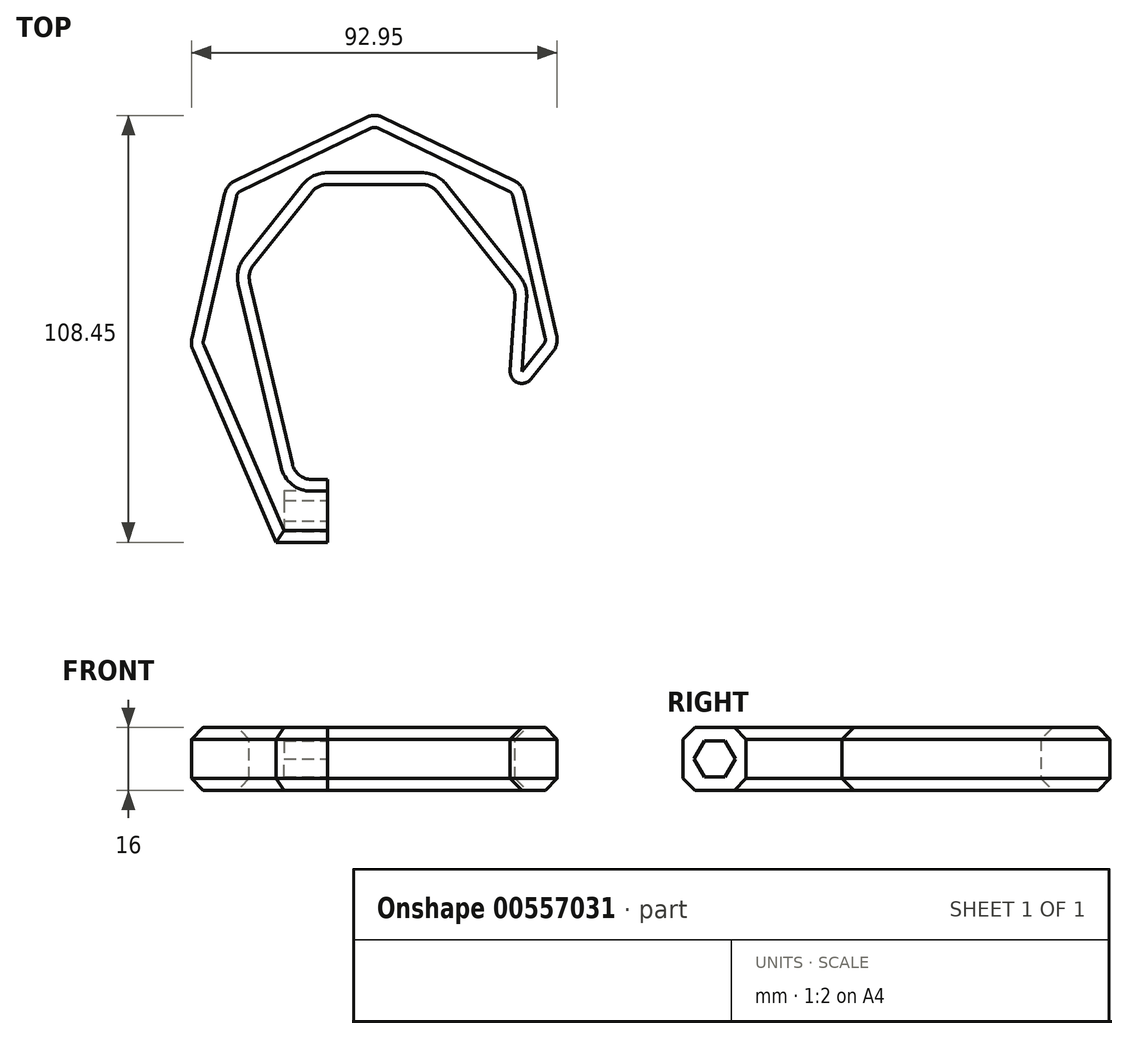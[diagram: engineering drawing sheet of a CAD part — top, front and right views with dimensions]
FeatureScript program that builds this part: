
annotation { "Feature Type Name" : "Feature", "Feature Type Description" : "" }
export const myFeature = defineFeature(function(context is Context, id is Id, definition is map)
    precondition{}
    {
        {
            var Q0;
            Q0=qCreatedBy(makeId("Top.planeOp"),FACE);
            var sketch = newSketch(context, id + "F0", { "sketchPlane" : qUnion([Q0])});
            skLineSegment(sketch, "E0", {"start": v(0, -45) * mm, "end": v(-20, -45) * mm});
            skLineSegment(sketch, "E1", {"start": v(0, -45) * mm, "end": v(0, -61) * mm});
            skLineSegment(sketch, "E2", {"start": v(0, -61) * mm, "end": v(-25, -61) * mm});
            skCircle(sketch, "E3.cCircle", {"center": v(0, 0) * mm, "radius": 43.25 * mm, "construction": true});
            skLineSegment(sketch, "E3.0", {"start": v(46.8, -10.68) * mm, "end": v(20.83, -43.25) * mm});
            skLineSegment(sketch, "E3.1", {"start": v(20.83, -43.25) * mm, "end": v(-20.83, -43.25) * mm});
            skLineSegment(sketch, "E3.2", {"start": v(-20.83, -43.25) * mm, "end": v(-46.8, -10.68) * mm});
            skLineSegment(sketch, "E3.3", {"start": v(-46.8, -10.68) * mm, "end": v(-37.53, 29.93) * mm});
            skLineSegment(sketch, "E3.4", {"start": v(-37.53, 29.93) * mm, "end": v(0, 48) * mm});
            skLineSegment(sketch, "E3.5", {"start": v(0, 48) * mm, "end": v(37.53, 29.93) * mm});
            skLineSegment(sketch, "E3.6", {"start": v(37.53, 29.93) * mm, "end": v(46.8, -10.68) * mm});
            skPoint(sketch, "E3.0.midPoint", {"position": v(33.81, -26.96) * mm});
            skLineSegment(sketch, "E4", {"start": v(-20, -45) * mm, "end": v(-37.53, 29.93) * mm});
            skLineSegment(sketch, "E5", {"start": v(-25, -61) * mm, "end": v(-46.8, -10.68) * mm});
            skLineSegment(sketch, "E6", {"start": v(-46.8, -10.68) * mm, "end": v(0, 48) * mm});
            skLineSegment(sketch, "E7", {"start": v(-37.53, 29.93) * mm, "end": v(37.53, 29.93) * mm});
            skLineSegment(sketch, "E8", {"start": v(0, 48) * mm, "end": v(46.8, -10.68) * mm});
            skLineSegment(sketch, "E9", {"start": v(37.53, 29.93) * mm, "end": v(33.81, -26.96) * mm});
            skSolve(sketch);
        }
        {
            var Q0;
            {var subQ4=sQuery(id+"F0.wireOp",EDGE,"E0");Q0=makeQuery(id+"F0.imprint","IMPRINT",FACE,{"disambiguationData":[TD([[makeQuery(id+"F0.imprint","IMPRINT",EDGE,{"derivedFrom":subQ4}),1.0]])]});}
            var Q1;
            {var subQ0=sQuery(id+"F0.wireOp",EDGE,"E3.2");Q1=makeQuery(id+"F0.imprint","IMPRINT",FACE,{"disambiguationData":[TD([[makeQuery(id+"F0.imprint","IMPRINT",EDGE,{"derivedFrom":subQ0}),-1.0]])]});}
            var Q2;
            {var subQ0=sQuery(id+"F0.wireOp",EDGE,"E3.3");Q2=makeQuery(id+"F0.imprint","IMPRINT",FACE,{"disambiguationData":[TD([[makeQuery(id+"F0.imprint","IMPRINT",EDGE,{"derivedFrom":subQ0}),-1.0]])]});}
            var Q3;
            {var subQ1=sQuery(id+"F0.wireOp",EDGE,"E4");var subQ3=sQuery(id+"F0.wireOp",EDGE,"E6");var subQ4=makeQuery(id+"F0.imprint","INTERSECT",VERTEX,{"derivedFrom":[subQ1,subQ3]});Q3=makeQuery(id+"F0.imprint","IMPRINT",FACE,{"disambiguationData":[TD([[makeQuery(id+"F0.imprint","IMPRINT",EDGE,{"disambiguationData":[TD([[subQ4,-1.0]])],"derivedFrom":subQ3}),1.0]])]});}
            var Q4;
            {var subQ0=sQuery(id+"F0.wireOp",EDGE,"E3.4");Q4=makeQuery(id+"F0.imprint","IMPRINT",FACE,{"disambiguationData":[TD([[makeQuery(id+"F0.imprint","IMPRINT",EDGE,{"derivedFrom":subQ0}),-1.0]])]});}
            var Q5;
            {var subQ1=sQuery(id+"F0.wireOp",EDGE,"E6");var subQ3=sQuery(id+"F0.wireOp",EDGE,"E7");var subQ4=makeQuery(id+"F0.imprint","INTERSECT",VERTEX,{"derivedFrom":[subQ1,subQ3]});Q5=makeQuery(id+"F0.imprint","IMPRINT",FACE,{"disambiguationData":[TD([[makeQuery(id+"F0.imprint","IMPRINT",EDGE,{"disambiguationData":[TD([[subQ4,-1.0]])],"derivedFrom":subQ3}),1.0]])]});}
            var Q6;
            {var subQ0=sQuery(id+"F0.wireOp",EDGE,"E3.5");Q6=makeQuery(id+"F0.imprint","IMPRINT",FACE,{"disambiguationData":[TD([[makeQuery(id+"F0.imprint","IMPRINT",EDGE,{"derivedFrom":subQ0}),-1.0]])]});}
            var Q7;
            {var subQ1=sQuery(id+"F0.wireOp",EDGE,"E7");var subQ3=sQuery(id+"F0.wireOp",EDGE,"E8");var subQ4=makeQuery(id+"F0.imprint","INTERSECT",VERTEX,{"derivedFrom":[subQ1,subQ3]});Q7=makeQuery(id+"F0.imprint","IMPRINT",FACE,{"disambiguationData":[TD([[makeQuery(id+"F0.imprint","IMPRINT",EDGE,{"disambiguationData":[TD([[subQ4,-1.0]])],"derivedFrom":subQ3}),1.0]])]});}
            var Q8;
            {var subQ0=sQuery(id+"F0.wireOp",EDGE,"E3.6");Q8=makeQuery(id+"F0.imprint","IMPRINT",FACE,{"disambiguationData":[TD([[makeQuery(id+"F0.imprint","IMPRINT",EDGE,{"derivedFrom":subQ0}),-1.0]])]});}
            var Q9;
            {var subQ1=sQuery(id+"F0.wireOp",EDGE,"E3.0");var subQ3=sQuery(id+"F0.wireOp",EDGE,"E9");var subQ4=makeQuery(id+"F0.imprint","INTERSECT",VERTEX,{"derivedFrom":[subQ1,subQ3]});Q9=makeQuery(id+"F0.imprint","IMPRINT",FACE,{"disambiguationData":[TD([[makeQuery(id+"F0.imprint","IMPRINT",EDGE,{"disambiguationData":[TD([[subQ4,1.0]])],"derivedFrom":subQ3}),1.0]])]});}
            extrude(context, id + "F1", {"entities" : qUnion([Q0, Q1, Q2, Q3, Q4, Q5, Q6, Q7, Q8, Q9]), "depth" : 16 * mm, "offsetDistance" : 25 * mm});
        }
        {
            var Q0;
            Q0=makeQuery(id+"F1.opExtrude","SWEPT_EDGE",EDGE,{"disambiguationData":[OSD([sQuery(id+"F0.wireOp",EDGE,"E3.0"),sQuery(id+"F0.wireOp",EDGE,"E9")])]});
            fillet(context, id + "F2", {"entities" : qUnion([Q0]), "radius" : 3 * mm, "tangentPropagation" : true, "allowEdgeOverflow" : false});
        }
        {
            var Q0;
            Q0=makeQuery(id+"F1.opExtrude","SWEPT_EDGE",EDGE,{"disambiguationData":[OSD([sQuery(id+"F0.wireOp",EDGE,"E3.2"),sQuery(id+"F0.wireOp",EDGE,"E3.3"),sQuery(id+"F0.wireOp",EDGE,"E5"),sQuery(id+"F0.wireOp",EDGE,"E6")])]});
            var Q1;
            Q1=makeQuery(id+"F1.opExtrude","SWEPT_EDGE",EDGE,{"disambiguationData":[OSD([sQuery(id+"F0.wireOp",EDGE,"E3.3"),sQuery(id+"F0.wireOp",EDGE,"E3.4"),sQuery(id+"F0.wireOp",EDGE,"E4"),sQuery(id+"F0.wireOp",EDGE,"E7")])]});
            var Q2;
            Q2=makeQuery(id+"F1.opExtrude","SWEPT_EDGE",EDGE,{"disambiguationData":[OSD([sQuery(id+"F0.wireOp",EDGE,"E3.4"),sQuery(id+"F0.wireOp",EDGE,"E3.5"),sQuery(id+"F0.wireOp",EDGE,"E6"),sQuery(id+"F0.wireOp",EDGE,"E8")])]});
            var Q3;
            Q3=makeQuery(id+"F1.opExtrude","SWEPT_EDGE",EDGE,{"disambiguationData":[OSD([sQuery(id+"F0.wireOp",EDGE,"E3.5"),sQuery(id+"F0.wireOp",EDGE,"E3.6"),sQuery(id+"F0.wireOp",EDGE,"E7"),sQuery(id+"F0.wireOp",EDGE,"E9")])]});
            var Q4;
            Q4=makeQuery(id+"F1.opExtrude","SWEPT_EDGE",EDGE,{"disambiguationData":[OSD([sQuery(id+"F0.wireOp",EDGE,"E3.0"),sQuery(id+"F0.wireOp",EDGE,"E3.6"),sQuery(id+"F0.wireOp",EDGE,"E8")])]});
            fillet(context, id + "F3", {"entities" : qUnion([Q0, Q1, Q2, Q3, Q4]), "radius" : 5 * mm, "tangentPropagation" : true, "allowEdgeOverflow" : false});
        }
        {
            var Q0;
            Q0=makeQuery(id+"F1.opExtrude","SWEPT_EDGE",EDGE,{"disambiguationData":[OSD([sQuery(id+"F0.wireOp",EDGE,"E4"),sQuery(id+"F0.wireOp",EDGE,"E6")])]});
            var Q1;
            Q1=makeQuery(id+"F1.opExtrude","SWEPT_EDGE",EDGE,{"disambiguationData":[OSD([sQuery(id+"F0.wireOp",EDGE,"E6"),sQuery(id+"F0.wireOp",EDGE,"E7")])]});
            var Q2;
            Q2=makeQuery(id+"F1.opExtrude","SWEPT_EDGE",EDGE,{"disambiguationData":[OSD([sQuery(id+"F0.wireOp",EDGE,"E7"),sQuery(id+"F0.wireOp",EDGE,"E8")])]});
            var Q3;
            Q3=makeQuery(id+"F1.opExtrude","SWEPT_EDGE",EDGE,{"disambiguationData":[OSD([sQuery(id+"F0.wireOp",EDGE,"E8"),sQuery(id+"F0.wireOp",EDGE,"E9")])]});
            var Q4;
            Q4=makeQuery(id+"F1.opExtrude","SWEPT_EDGE",EDGE,{"disambiguationData":[OSD([sQuery(id+"F0.wireOp",EDGE,"E0"),sQuery(id+"F0.wireOp",EDGE,"E4")])]});
            fillet(context, id + "F4", {"entities" : qUnion([Q0, Q1, Q2, Q3, Q4]), "radius" : 5 * mm, "tangentPropagation" : true, "allowEdgeOverflow" : false});
        }
        {
            var Q0;
            Q0=makeQuery(id+"F1.opExtrude","SWEPT_FACE",FACE,{"disambiguationData":[OSD([sQuery(id+"F0.wireOp",EDGE,"E1")])]});
            var sketch = newSketch(context, id + "F5", { "sketchPlane" : qUnion([Q0])});
            skCircle(sketch, "E10.cCircle", {"center": v(-53, 8) * mm, "radius": 4.53 * mm, "construction": true});
            skLineSegment(sketch, "E10.0", {"start": v(-55.61, 3.48) * mm, "end": v(-58.23, 8) * mm});
            skLineSegment(sketch, "E10.1", {"start": v(-58.23, 8) * mm, "end": v(-55.61, 12.53) * mm});
            skLineSegment(sketch, "E10.2", {"start": v(-55.61, 12.53) * mm, "end": v(-50.39, 12.52) * mm});
            skLineSegment(sketch, "E10.3", {"start": v(-50.39, 12.52) * mm, "end": v(-47.77, 8) * mm});
            skLineSegment(sketch, "E10.4", {"start": v(-47.77, 8) * mm, "end": v(-50.39, 3.47) * mm});
            skLineSegment(sketch, "E10.5", {"start": v(-50.39, 3.47) * mm, "end": v(-55.61, 3.48) * mm});
            skPoint(sketch, "E10.0.midPoint", {"position": v(-56.92, 5.74) * mm});
            skLineSegment(sketch, "E11", {"start": v(-53, 8) * mm, "end": v(-53, 0) * mm, "construction": true});
            skLineSegment(sketch, "E12", {"start": v(-53, 8) * mm, "end": v(-53, 16) * mm, "construction": true});
            skLineSegment(sketch, "E13", {"start": v(-45, 8) * mm, "end": v(-53, 8) * mm, "construction": true});
            skLineSegment(sketch, "E14", {"start": v(-61, 8) * mm, "end": v(-53, 8) * mm, "construction": true});
            skSolve(sketch);
        }
        {
            var Q0;
            Q0=makeQuery(id+"F5.imprint","IMPRINT",FACE,{"disambiguationData":[TD([[makeQuery(id+"F5.imprint","IMPRINT",EDGE,{"derivedFrom":sQuery(id+"F5.wireOp",EDGE,"E10.0")}),1.0]])]});
            var Q1;
            Q1=makeQuery(id+"F5.imprint","IMPRINT",FACE,{"disambiguationData":[TD([[makeQuery(id+"F5.imprint","IMPRINT",EDGE,{"derivedFrom":sQuery(id+"F5.wireOp",EDGE,"E10.0")}),-1.0]])]});
            extrude(context, id + "F6", {"entities" : qUnion([Q0, Q1]), "operationType" : NewBodyOperationType.REMOVE, "oppositeDirection" : true, "depth" : 12 * mm, "offsetDistance" : 25 * mm});
        }
        {
            var Q0;
            Q0=makeQuery(id+"F5.imprint","IMPRINT",FACE,{"disambiguationData":[TD([[makeQuery(id+"F5.imprint","IMPRINT",EDGE,{"derivedFrom":sQuery(id+"F5.wireOp",EDGE,"E10.0")}),-1.0]])]});
            extrude(context, id + "F7", {"entities" : qUnion([Q0]), "operationType" : NewBodyOperationType.REMOVE, "oppositeDirection" : true, "depth" : (11 + 12) * mm, "offsetDistance" : 25 * mm});
        }
        {
            var Q0;
            Q0=makeQuery(id+"F1.opExtrude","CAP_EDGE",EDGE,{"disambiguationData":[OSD([sQuery(id+"F0.wireOp",EDGE,"E4")])],"isStart":false});
            var Q1;
            Q1=makeQuery(id+"F1.opExtrude","CAP_EDGE",EDGE,{"disambiguationData":[OSD([sQuery(id+"F0.wireOp",EDGE,"E2")])],"isStart":false});
            var Q2;
            Q2=makeQuery(id+"F1.opExtrude","CAP_EDGE",EDGE,{"disambiguationData":[OSD([sQuery(id+"F0.wireOp",EDGE,"E2")])],"isStart":true});
            var Q3;
            Q3=makeQuery(id+"F1.opExtrude","CAP_EDGE",EDGE,{"disambiguationData":[OSD([sQuery(id+"F0.wireOp",EDGE,"E4")])],"isStart":true});
            chamfer(context, id + "F8", {"entities" : qUnion([Q0, Q1, Q2, Q3]), "width" : 3 * mm, "tangentPropagation" : true});
        }
    });
